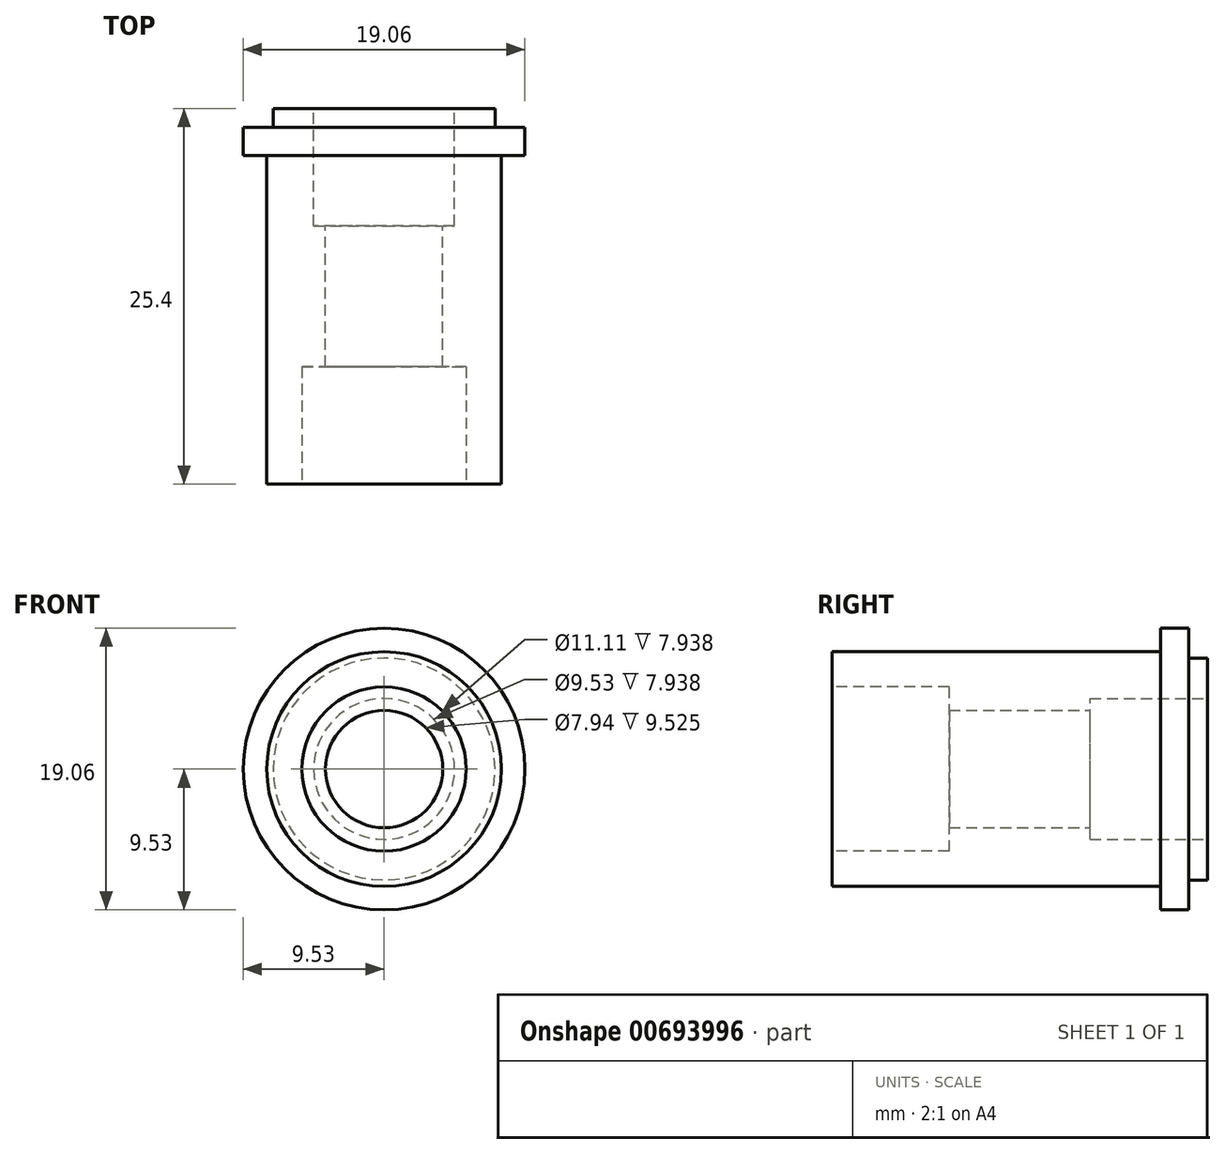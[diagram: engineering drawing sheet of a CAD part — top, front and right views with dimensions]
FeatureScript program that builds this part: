
annotation { "Feature Type Name" : "Feature", "Feature Type Description" : "" }
export const myFeature = defineFeature(function(context is Context, id is Id, definition is map)
    precondition{}
    {
        {
            var Q0;
            Q0=qCreatedBy(makeId("Front.planeOp"),FACE);
            var sketch = newSketch(context, id + "F0", { "sketchPlane" : qUnion([Q0])});
            skCircle(sketch, "E0", {"center": v(0, 0) * mm, "radius": 4.76 * mm});
            skCircle(sketch, "E1", {"center": v(0, 0) * mm, "radius": 9.53 * mm});
            skCircle(sketch, "E2", {"center": v(0, 0) * mm, "radius": 7.5 * mm});
            skSolve(sketch);
        }
        {
            var Q0;
            Q0=makeQuery(id+"F0.imprint","IMPRINT",FACE,{"disambiguationData":[TD([[makeQuery(id+"F0.imprint","IMPRINT",EDGE,{"derivedFrom":sQuery(id+"F0.wireOp",EDGE,"E1")}),1.0]])]});
            var Q1;
            Q1=makeQuery(id+"F0.imprint","IMPRINT",FACE,{"disambiguationData":[TD([[makeQuery(id+"F0.imprint","IMPRINT",EDGE,{"derivedFrom":sQuery(id+"F0.wireOp",EDGE,"E0")}),1.0]])]});
            var Q2;
            Q2=makeQuery(id+"F0.imprint","IMPRINT",FACE,{"disambiguationData":[TD([[makeQuery(id+"F0.imprint","IMPRINT",EDGE,{"derivedFrom":sQuery(id+"F0.wireOp",EDGE,"E0")}),-1.0]])]});
            extrude(context, id + "F1", {"entities" : qUnion([Q0, Q1, Q2]), "depth" : 25.4 * mm, "offsetDistance" : 25.4 * mm});
        }
        {
            var Q0;
            Q0=makeQuery(id+"F1.opExtrude","CAP_FACE",FACE,{"disambiguationData":[OSD([sQuery(id+"F0.wireOp",EDGE,"E1")])],"isStart":false});
            var sketch = newSketch(context, id + "F2", { "sketchPlane" : qUnion([Q0])});
            skCircle(sketch, "E3", {"center": v(0, 0) * mm, "radius": 5.56 * mm});
            skCircle(sketch, "E4", {"center": v(0, 0) * mm, "radius": 7.94 * mm});
            skSolve(sketch);
        }
        {
            var Q0;
            Q0=makeQuery(id+"F2.imprint","IMPRINT",FACE,{"disambiguationData":[TD([[makeQuery(id+"F2.imprint","IMPRINT",EDGE,{"derivedFrom":sQuery(id+"F2.wireOp",EDGE,"E3")}),1.0]])]});
            extrude(context, id + "F3", {"entities" : qUnion([Q0]), "operationType" : NewBodyOperationType.REMOVE, "oppositeDirection" : true, "depth" : 7.94 * mm, "offsetDistance" : 25.4 * mm});
        }
        {
            var Q0;
            Q0=makeQuery(id+"F3.boolean.opBoolean","COPY",FACE,{"derivedFrom":makeQuery(id+"F3.opExtrude","CAP_FACE",FACE,{"disambiguationData":[OSD([sQuery(id+"F2.wireOp",EDGE,"E3")])],"isStart":false})});
            var sketch = newSketch(context, id + "F4", { "sketchPlane" : qUnion([Q0])});
            skPoint(sketch, "E5", {"position": v(0, 0) * mm});
            skSolve(sketch);
        }
        {
            var Q0;
            Q0=makeQuery(id+"F2.imprint","IMPRINT",FACE,{"disambiguationData":[TD([[makeQuery(id+"F2.imprint","IMPRINT",EDGE,{"derivedFrom":sQuery(id+"F2.wireOp",EDGE,"E4")}),-1.0]])]});
            extrude(context, id + "F5", {"entities" : qUnion([Q0]), "operationType" : NewBodyOperationType.REMOVE, "oppositeDirection" : true, "depth" : 22.22 * mm, "offsetDistance" : 25.4 * mm});
        }
        {
            var Q0;
            Q0=makeQuery(id+"F0.imprint","IMPRINT",FACE,{"disambiguationData":[TD([[makeQuery(id+"F0.imprint","IMPRINT",EDGE,{"derivedFrom":sQuery(id+"F0.wireOp",EDGE,"E1")}),1.0]])]});
            extrude(context, id + "F6", {"entities" : qUnion([Q0]), "operationType" : NewBodyOperationType.REMOVE, "depth" : 1.27 * mm, "offsetDistance" : 25.4 * mm});
        }
        {
            var Q0;
            Q0=makeQuery(id+"F0.imprint","IMPRINT",FACE,{"disambiguationData":[TD([[makeQuery(id+"F0.imprint","IMPRINT",EDGE,{"derivedFrom":sQuery(id+"F0.wireOp",EDGE,"E0")}),1.0]])]});
            extrude(context, id + "F7", {"entities" : qUnion([Q0]), "operationType" : NewBodyOperationType.REMOVE, "depth" : 7.94 * mm, "offsetDistance" : 25.4 * mm});
        }
        {
            var Q0;
            Q0=sQuery(id+"F4.wireOp",VERTEX,"E5");
            var Q1;
            Q1=makeQuery(id+"F1.opExtrude","SWEPT_BODY",BODY,{"disambiguationData":[OSD([sQuery(id+"F0.wireOp",EDGE,"E1")])]});
            hole(context, id + "F8", {"style" : HoleStyle.SIMPLE, "endStyle" : HoleEndStyle.THROUGH, "holeDiameter" : 7.94 * mm, "majorDiameter" : 6.35 * mm, "isTappedThrough" : true, "tappedDepth" : 12.7 * mm, "tapClearance" : 3, "locations" : qUnion([Q0]), "scope" : qUnion([Q1]), "startStyle" : HoleStartStyle.PART});
        }
    });
